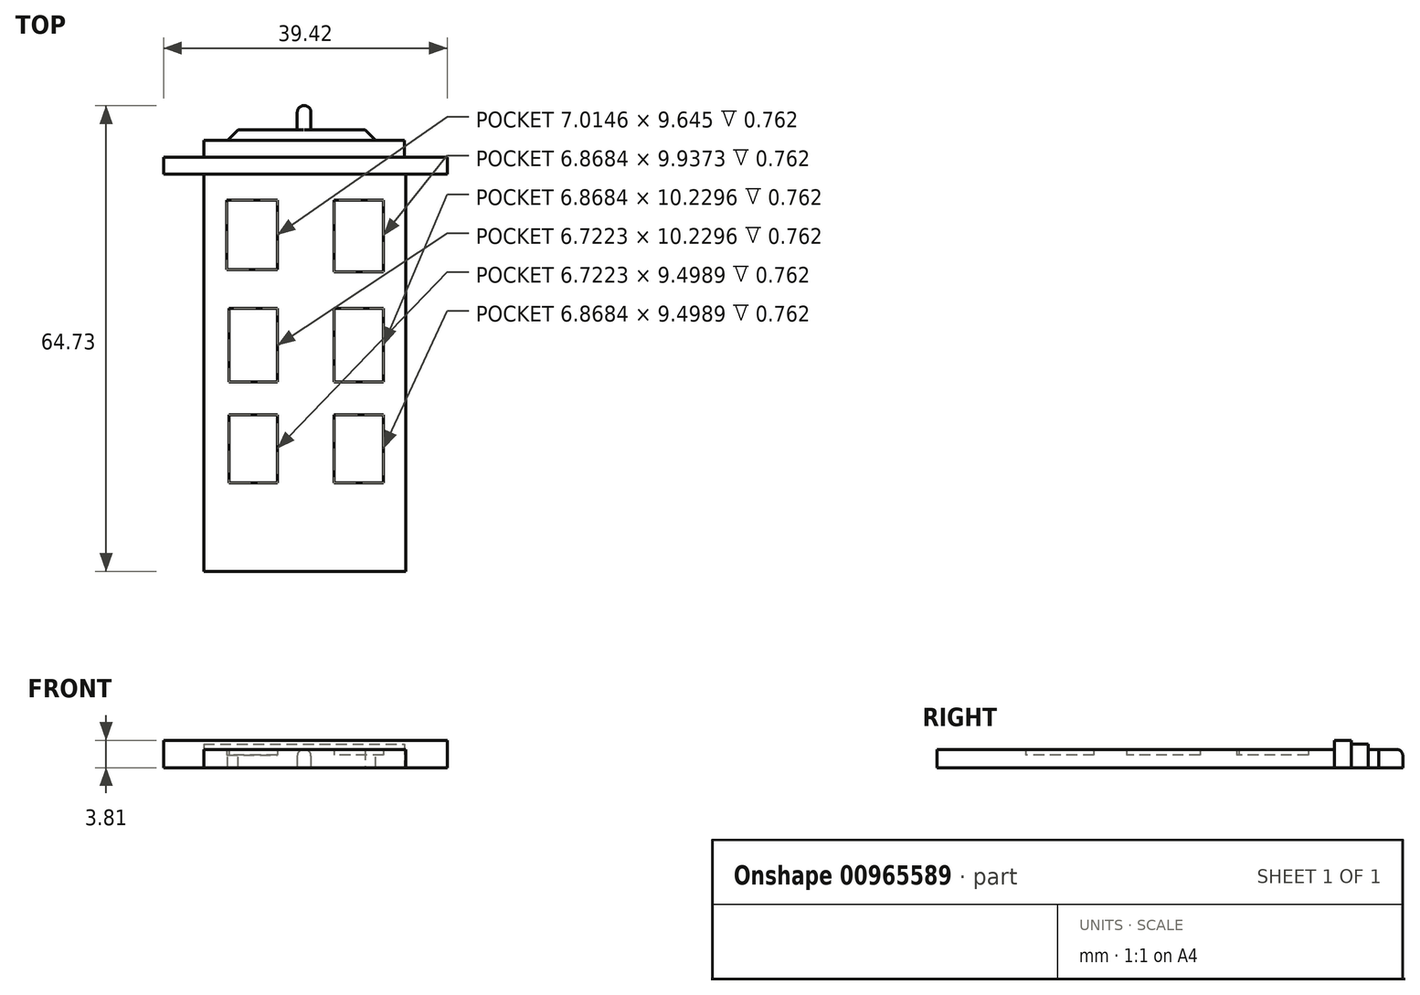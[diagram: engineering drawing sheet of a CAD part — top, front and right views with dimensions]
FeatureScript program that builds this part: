
annotation { "Feature Type Name" : "Feature", "Feature Type Description" : "" }
export const myFeature = defineFeature(function(context is Context, id is Id, definition is map)
    precondition{}
    {
        {
            var Q0;
            Q0=qCreatedBy(makeId("Top.planeOp"),FACE);
            var sketch = newSketch(context, id + "F0", { "sketchPlane" : qUnion([Q0])});
            skLineSegment(sketch, "E0.bottom", {"start": v(-69.78, 53.05) * mm, "end": v(-41.72, 53.05) * mm});
            skLineSegment(sketch, "E0.top", {"start": v(-69.78, -2.2) * mm, "end": v(-41.72, -2.2) * mm});
            skLineSegment(sketch, "E0.left", {"start": v(-69.78, 53.05) * mm, "end": v(-69.78, -2.2) * mm});
            skLineSegment(sketch, "E0.right", {"start": v(-41.72, 53.05) * mm, "end": v(-41.72, -2.2) * mm});
            skLineSegment(sketch, "E1.bottom", {"start": v(-66.57, 49.4) * mm, "end": v(-59.55, 49.4) * mm});
            skLineSegment(sketch, "E1.top", {"start": v(-66.57, 39.75) * mm, "end": v(-59.55, 39.75) * mm});
            skLineSegment(sketch, "E1.left", {"start": v(-66.57, 49.4) * mm, "end": v(-66.57, 39.75) * mm});
            skLineSegment(sketch, "E1.right", {"start": v(-59.55, 49.4) * mm, "end": v(-59.55, 39.75) * mm});
            skPoint(sketch, "E2.firstSnap0", {"position": v(-63.06, 49.4) * mm});
            skLineSegment(sketch, "E2.bottom", {"start": v(-44.8, 49.4) * mm, "end": v(-51.66, 49.4) * mm});
            skLineSegment(sketch, "E2.top", {"start": v(-44.8, 39.46) * mm, "end": v(-51.66, 39.46) * mm});
            skLineSegment(sketch, "E2.left", {"start": v(-44.8, 49.4) * mm, "end": v(-44.8, 39.46) * mm});
            skLineSegment(sketch, "E2.right", {"start": v(-51.66, 49.4) * mm, "end": v(-51.66, 39.46) * mm});
            skLineSegment(sketch, "E3.bottom", {"start": v(-51.66, 34.34) * mm, "end": v(-44.8, 34.34) * mm});
            skLineSegment(sketch, "E3.top", {"start": v(-51.66, 24.11) * mm, "end": v(-44.8, 24.11) * mm});
            skLineSegment(sketch, "E3.left", {"start": v(-51.66, 34.34) * mm, "end": v(-51.66, 24.11) * mm});
            skLineSegment(sketch, "E3.right", {"start": v(-44.8, 34.34) * mm, "end": v(-44.8, 24.11) * mm});
            skLineSegment(sketch, "E4.bottom", {"start": v(-59.55, 34.34) * mm, "end": v(-66.27, 34.34) * mm});
            skLineSegment(sketch, "E4.top", {"start": v(-59.55, 24.11) * mm, "end": v(-66.27, 24.11) * mm});
            skLineSegment(sketch, "E4.left", {"start": v(-59.55, 34.34) * mm, "end": v(-59.55, 24.11) * mm});
            skLineSegment(sketch, "E4.right", {"start": v(-66.27, 34.34) * mm, "end": v(-66.27, 24.11) * mm});
            skLineSegment(sketch, "E5.bottom", {"start": v(-59.55, 19.58) * mm, "end": v(-66.27, 19.58) * mm});
            skLineSegment(sketch, "E5.top", {"start": v(-59.55, 10.08) * mm, "end": v(-66.27, 10.08) * mm});
            skLineSegment(sketch, "E5.left", {"start": v(-59.55, 19.58) * mm, "end": v(-59.55, 10.08) * mm});
            skLineSegment(sketch, "E5.right", {"start": v(-66.27, 19.58) * mm, "end": v(-66.27, 10.08) * mm});
            skLineSegment(sketch, "E6.bottom", {"start": v(-51.66, 19.58) * mm, "end": v(-44.8, 19.58) * mm});
            skLineSegment(sketch, "E6.top", {"start": v(-51.66, 10.08) * mm, "end": v(-44.8, 10.08) * mm});
            skLineSegment(sketch, "E6.left", {"start": v(-51.66, 19.58) * mm, "end": v(-51.66, 10.08) * mm});
            skLineSegment(sketch, "E6.right", {"start": v(-44.8, 19.58) * mm, "end": v(-44.8, 10.08) * mm});
            skLineSegment(sketch, "E7.bottom", {"start": v(-75.36, 53.05) * mm, "end": v(-35.94, 53.05) * mm});
            skLineSegment(sketch, "E7.top", {"start": v(-75.36, 55.39) * mm, "end": v(-35.94, 55.39) * mm});
            skLineSegment(sketch, "E7.left", {"start": v(-75.36, 53.05) * mm, "end": v(-75.36, 55.39) * mm});
            skLineSegment(sketch, "E7.right", {"start": v(-35.94, 53.05) * mm, "end": v(-35.94, 55.39) * mm});
            skLineSegment(sketch, "E8.bottom", {"start": v(-69.78, 55.39) * mm, "end": v(-41.88, 55.39) * mm});
            skLineSegment(sketch, "E8.top", {"start": v(-69.78, 57.72) * mm, "end": v(-41.88, 57.72) * mm});
            skLineSegment(sketch, "E8.left", {"start": v(-69.78, 55.39) * mm, "end": v(-69.78, 57.72) * mm});
            skLineSegment(sketch, "E8.right", {"start": v(-41.88, 55.39) * mm, "end": v(-41.88, 57.72) * mm});
            skLineSegment(sketch, "E9", {"start": v(-55.83, 57.72) * mm, "end": v(-55.83, 62.54) * mm});
            skLineSegment(sketch, "E10.bottom", {"start": v(-56.78, 57.72) * mm, "end": v(-54.88, 57.72) * mm});
            skLineSegment(sketch, "E10.top", {"start": v(-56.78, 62.54) * mm, "end": v(-54.88, 62.54) * mm});
            skLineSegment(sketch, "E10.left", {"start": v(-56.78, 57.72) * mm, "end": v(-56.78, 62.54) * mm});
            skLineSegment(sketch, "E10.right", {"start": v(-54.88, 57.72) * mm, "end": v(-54.88, 62.54) * mm});
            skLineSegment(sketch, "E11.bottom", {"start": v(-67.55, 57.72) * mm, "end": v(-44.82, 57.72) * mm});
            skLineSegment(sketch, "E11.top", {"start": v(-67.55, 59.17) * mm, "end": v(-44.82, 59.17) * mm});
            skLineSegment(sketch, "E11.left", {"start": v(-67.55, 57.72) * mm, "end": v(-67.55, 59.17) * mm});
            skLineSegment(sketch, "E11.right", {"start": v(-44.82, 57.72) * mm, "end": v(-44.82, 59.17) * mm});
            skSolve(sketch);
        }
        {
            var Q0;
            {var subQ0=sQuery(id+"F0.wireOp",EDGE,"E9");var subQ1=sQuery(id+"F0.wireOp",EDGE,"E8.top");var subQ2=makeQuery(id+"F0.imprint","INTERSECT",VERTEX,{"derivedFrom":[subQ1,subQ0]});var subQ5=makeQuery(id+"F0.imprint","IMPRINT",EDGE,{"disambiguationData":[TD([[subQ2,1.0]])],"derivedFrom":subQ1});var subQ6=sQuery(id+"F0.wireOp",EDGE,"E11.top");var subQ7=makeQuery(id+"F0.imprint","INTERSECT",VERTEX,{"derivedFrom":[subQ0,subQ6]});var subQ12=sQuery(id+"F0.wireOp",EDGE,"E11.right");var subQ19=makeQuery(id+"F0.imprint","IMPRINT",EDGE,{"disambiguationData":[TD([[subQ2,-1.0]])],"derivedFrom":subQ1});var subQ21=sQuery(id+"F0.wireOp",EDGE,"E11.left");var subQ26=sQuery(id+"F0.wireOp",EDGE,"E0.bottom");var subQ27=makeQuery(id+"F0.imprint","IMPRINT",EDGE,{"derivedFrom":subQ26});var subQ30=makeQuery(id+"F0.imprint","IMPRINT",EDGE,{"disambiguationData":[TD([[subQ7,-1.0]])],"derivedFrom":subQ0});var subQ35=sQuery(id+"F0.wireOp",EDGE,"E8.left");Q0=qUnion([makeQuery(id+"F0.imprint","IMPRINT",FACE,{"disambiguationData":[TD([[subQ30,-1.0]])]}),makeQuery(id+"F0.imprint","IMPRINT",FACE,{"disambiguationData":[TD([[makeQuery(id+"F0.imprint","IMPRINT",EDGE,{"derivedFrom":subQ35}),-1.0]])]}),makeQuery(id+"F0.imprint","IMPRINT",FACE,{"disambiguationData":[TD([[subQ27,1.0]])]}),makeQuery(id+"F0.imprint","IMPRINT",FACE,{"disambiguationData":[TD([[subQ30,1.0]])]}),makeQuery(id+"F0.imprint","IMPRINT",FACE,{"disambiguationData":[TD([[subQ27,-1.0]])]}),makeQuery(id+"F0.imprint","IMPRINT",FACE,{"disambiguationData":[TD([[makeQuery(id+"F0.imprint","IMPRINT",EDGE,{"derivedFrom":subQ21}),-1.0]])]}),makeQuery(id+"F0.imprint","IMPRINT",FACE,{"disambiguationData":[TD([[subQ19,1.0]])]}),makeQuery(id+"F0.imprint","IMPRINT",FACE,{"disambiguationData":[TD([[makeQuery(id+"F0.imprint","IMPRINT",EDGE,{"derivedFrom":subQ12}),1.0]])]}),makeQuery(id+"F0.imprint","IMPRINT",FACE,{"disambiguationData":[TD([[subQ5,1.0]])]})]);}
            extrude(context, id + "F1", {"entities" : qUnion([Q0]), "depth" : 2.54 * mm, "offsetDistance" : 25.4 * mm});
        }
        {
            var Q0;
            Q0=makeQuery(id+"F1.opExtrude","CAP_EDGE",EDGE,{"disambiguationData":[OSD([sQuery(id+"F0.wireOp",EDGE,"E10.right")])],"isStart":false});
            var Q1;
            Q1=makeQuery(id+"F1.opExtrude","CAP_EDGE",EDGE,{"disambiguationData":[OSD([sQuery(id+"F0.wireOp",EDGE,"E10.left")])],"isStart":false});
            var Q2;
            Q2=makeQuery(id+"F1.opExtrude","CAP_EDGE",EDGE,{"disambiguationData":[OSD([sQuery(id+"F0.wireOp",EDGE,"E10.top")])],"isStart":false});
            var Q3;
            Q3=makeQuery(id+"F1.opExtrude","SWEPT_EDGE",EDGE,{"disambiguationData":[OSD([sQuery(id+"F0.wireOp",EDGE,"E10.top"),sQuery(id+"F0.wireOp",EDGE,"E10.left")])]});
            var Q4;
            Q4=makeQuery(id+"F1.opExtrude","SWEPT_EDGE",EDGE,{"disambiguationData":[OSD([sQuery(id+"F0.wireOp",EDGE,"E10.top"),sQuery(id+"F0.wireOp",EDGE,"E10.right")])]});
            fillet(context, id + "F2", {"entities" : qUnion([Q0, Q1, Q2, Q3, Q4]), "radius" : 0.89 * mm, "tangentPropagation" : true, "allowEdgeOverflow" : false});
        }
        {
            var Q0;
            Q0=makeQuery(id+"F0.imprint","IMPRINT",FACE,{"disambiguationData":[TD([[makeQuery(id+"F0.imprint","IMPRINT",EDGE,{"derivedFrom":sQuery(id+"F0.wireOp",EDGE,"E1.bottom")}),-1.0]])]});
            var Q1;
            Q1=makeQuery(id+"F0.imprint","IMPRINT",FACE,{"disambiguationData":[TD([[makeQuery(id+"F0.imprint","IMPRINT",EDGE,{"derivedFrom":sQuery(id+"F0.wireOp",EDGE,"E2.bottom")}),1.0]])]});
            var Q2;
            Q2=makeQuery(id+"F0.imprint","IMPRINT",FACE,{"disambiguationData":[TD([[makeQuery(id+"F0.imprint","IMPRINT",EDGE,{"derivedFrom":sQuery(id+"F0.wireOp",EDGE,"E4.bottom")}),1.0]])]});
            var Q3;
            Q3=makeQuery(id+"F0.imprint","IMPRINT",FACE,{"disambiguationData":[TD([[makeQuery(id+"F0.imprint","IMPRINT",EDGE,{"derivedFrom":sQuery(id+"F0.wireOp",EDGE,"E3.bottom")}),-1.0]])]});
            var Q4;
            Q4=makeQuery(id+"F0.imprint","IMPRINT",FACE,{"disambiguationData":[TD([[makeQuery(id+"F0.imprint","IMPRINT",EDGE,{"derivedFrom":sQuery(id+"F0.wireOp",EDGE,"E6.bottom")}),-1.0]])]});
            var Q5;
            Q5=makeQuery(id+"F0.imprint","IMPRINT",FACE,{"disambiguationData":[TD([[makeQuery(id+"F0.imprint","IMPRINT",EDGE,{"derivedFrom":sQuery(id+"F0.wireOp",EDGE,"E5.bottom")}),1.0]])]});
            extrude(context, id + "F3", {"entities" : qUnion([Q0, Q1, Q2, Q3, Q4, Q5]), "operationType" : NewBodyOperationType.ADD, "depth" : 1.78 * mm, "offsetDistance" : 25.4 * mm});
        }
        {
            var Q0;
            Q0=makeQuery(id+"F1.opExtrude","SWEPT_EDGE",EDGE,{"disambiguationData":[OSD([sQuery(id+"F0.wireOp",EDGE,"E11.top"),sQuery(id+"F0.wireOp",EDGE,"E11.left")])]});
            var Q1;
            Q1=makeQuery(id+"F1.opExtrude","SWEPT_EDGE",EDGE,{"disambiguationData":[OSD([sQuery(id+"F0.wireOp",EDGE,"E11.top"),sQuery(id+"F0.wireOp",EDGE,"E11.right")])]});
            chamfer(context, id + "F4", {"entities" : qUnion([Q0, Q1]), "width" : 2.54 * mm, "tangentPropagation" : true});
        }
        {
            var Q0;
            {var subQ1=sQuery(id+"F0.wireOp",EDGE,"E0.bottom");Q0=makeQuery(id+"F0.imprint","IMPRINT",FACE,{"disambiguationData":[TD([[makeQuery(id+"F0.imprint","IMPRINT",EDGE,{"derivedFrom":subQ1}),1.0]])]});}
            extrude(context, id + "F5", {"entities" : qUnion([Q0]), "operationType" : NewBodyOperationType.ADD, "depth" : 3.8 * mm, "offsetDistance" : 25.4 * mm});
        }
        {
            var Q0;
            {var subQ6=sQuery(id+"F0.wireOp",EDGE,"E8.left");Q0=makeQuery(id+"F0.imprint","IMPRINT",FACE,{"disambiguationData":[TD([[makeQuery(id+"F0.imprint","IMPRINT",EDGE,{"derivedFrom":subQ6}),-1.0]])]});}
            extrude(context, id + "F6", {"entities" : qUnion([Q0]), "operationType" : NewBodyOperationType.ADD, "depth" : 3.3 * mm, "offsetDistance" : 25.4 * mm});
        }
    });
